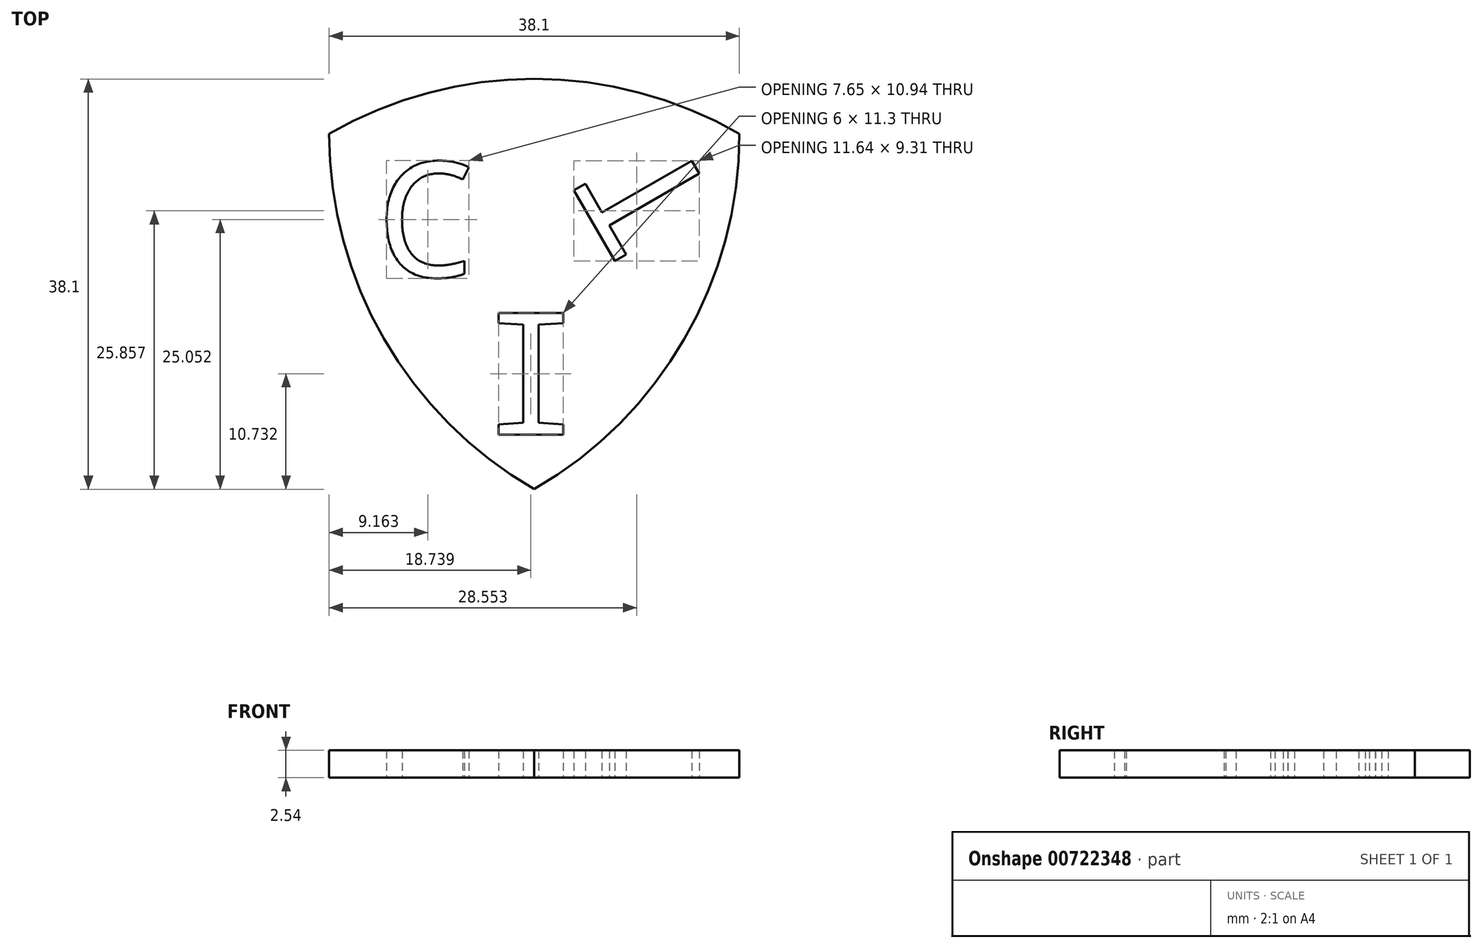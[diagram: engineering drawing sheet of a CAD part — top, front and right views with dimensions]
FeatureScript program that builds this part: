
annotation { "Feature Type Name" : "Feature", "Feature Type Description" : "" }
export const myFeature = defineFeature(function(context is Context, id is Id, definition is map)
    precondition{}
    {
        {
            var Q0;
            Q0=qCreatedBy(makeId("Top.planeOp"),FACE);
            var sketch = newSketch(context, id + "F0", { "sketchPlane" : qUnion([Q0])});
            skCircle(sketch, "E0", {"center": v(0, 0) * mm, "radius": 38.1 * mm});
            skSolve(sketch);
        }
        {
            var Q0;
            Q0=qCreatedBy(makeId("Top.planeOp"),FACE);
            var sketch = newSketch(context, id + "F1", { "sketchPlane" : qUnion([Q0])});
            skCircle(sketch, "E1", {"center": v(-38.1, 0) * mm, "radius": 38.1 * mm});
            skSolve(sketch);
        }
        {
            var Q0;
            Q0=qCreatedBy(makeId("Top.planeOp"),FACE);
            var sketch = newSketch(context, id + "F2", { "sketchPlane" : qUnion([Q0])});
            skCircle(sketch, "E2", {"center": v(-19.05, -33) * mm, "radius": 38.1 * mm});
            skSolve(sketch);
        }
        {
            var Q0;
            Q0 = qSketchRegion(id + "F0", true);
            extrude(context, id + "F3", {"entities" : qUnion([Q0]), "depth" : 2.54 * mm, "offsetDistance" : 25.4 * mm});
        }
        {
            var Q0;
            Q0 = qSketchRegion(id + "F1", true);
            extrude(context, id + "F4", {"entities" : qUnion([Q0]), "depth" : 2.54 * mm, "offsetDistance" : 25.4 * mm});
        }
        {
            var Q0;
            Q0 = qSketchRegion(id + "F2", true);
            extrude(context, id + "F5", {"entities" : qUnion([Q0]), "depth" : 2.54 * mm, "offsetDistance" : 25.4 * mm});
        }
        {
            var Q0;
            Q0=makeQuery(id+"F3.opExtrude","SWEPT_BODY",BODY,{"disambiguationData":[OSD([sQuery(id+"F0.wireOp",EDGE,"E0")])]});
            var Q1;
            Q1=makeQuery(id+"F4.opExtrude","SWEPT_BODY",BODY,{"disambiguationData":[OSD([sQuery(id+"F1.wireOp",EDGE,"E1")])]});
            var Q2;
            Q2=makeQuery(id+"F5.opExtrude","SWEPT_BODY",BODY,{"disambiguationData":[OSD([sQuery(id+"F2.wireOp",EDGE,"E2")])]});
            booleanBodies(context, id + "F6", {"operationType" : BooleanOperationType.INTERSECTION, "tools" : qUnion([Q0, Q1, Q2])});
        }
        {
            var Q0;
            Q0=qCreatedBy(makeId("Top.planeOp"),FACE);
            var sketch = newSketch(context, id + "F7", { "sketchPlane" : qUnion([Q0])});
            skText(sketch, "E3", { "text": "C", "fontName": "DroidSansMono.ttf"});
            skText(sketch, "E4", { "text": "I", "fontName": "DroidSansMono.ttf"});
            skText(sketch, "E5", { "text": "T", "fontName": "DroidSansMono.ttf"});
            const initialGuessF7  = {"E3": [-0.0337, -0.01327, 1, 0, 0.01073], "E4": [-0.0241, -0.02792, 1, 0, 0.0114], "E5": [-0.0018, -0.00703, -0.5, 0.86603, 0.01094]};
            skSetInitialGuess(sketch, initialGuessF7);
            skSolve(sketch);
        }
        {
            var Q0;
            Q0 = qSketchRegion(id + "F7", true);
            extrude(context, id + "F8", {"entities" : qUnion([Q0]), "operationType" : NewBodyOperationType.REMOVE, "depth" : 2.54 * mm, "offsetDistance" : 25.4 * mm});
        }
    });
